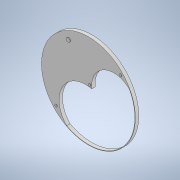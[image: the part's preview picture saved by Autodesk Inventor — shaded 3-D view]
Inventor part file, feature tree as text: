
AUTODESK INVENTOR PART (.ipt)
format: ipt  version: 2021 (Build 250183000, 183)  size: 125,440 bytes
history: native  units: mm
features: extrude x2, sketch x2
ambient origin geometry x8: Origin, YZ Plane, XZ Plane, XY Plane, X Axis, Y Axis, Z Axis, Center Point
bodies: Body1 (feature_tree)
feature tree (4):
  extrude  "Cadran"  Depth=54.0mm
  extrude  "Emplacements Vis"  Depth=54.5mm
  sketch  "Esquisse1"
  sketch  "Esquisse4"
